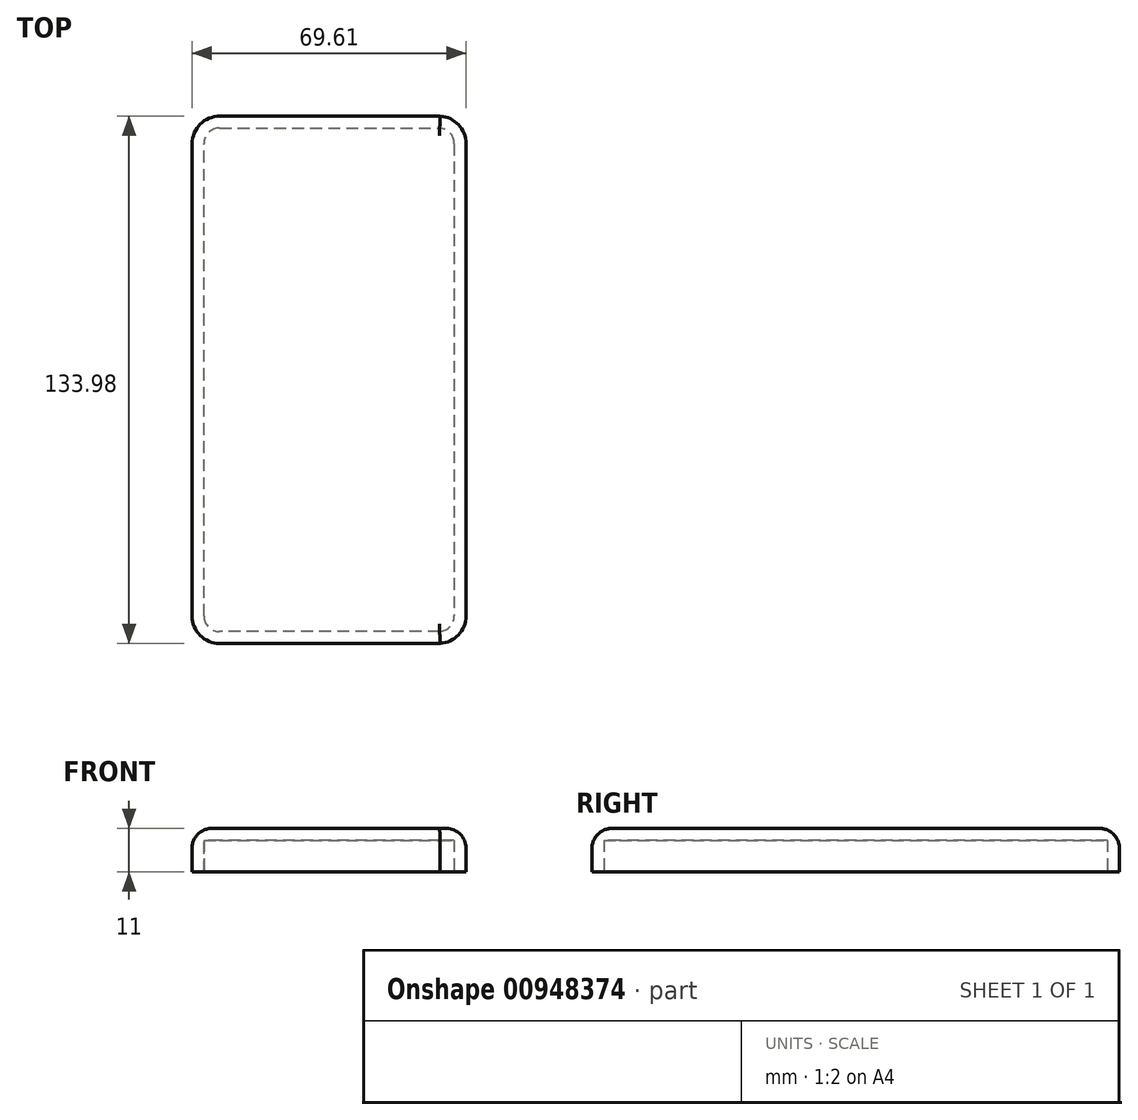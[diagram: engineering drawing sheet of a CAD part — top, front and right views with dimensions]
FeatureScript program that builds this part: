
annotation { "Feature Type Name" : "Feature", "Feature Type Description" : "" }
export const myFeature = defineFeature(function(context is Context, id is Id, definition is map)
    precondition{}
    {
        {
            var Q0;
            Q0=qCreatedBy(makeId("Top.planeOp"),FACE);
            var sketch = newSketch(context, id + "F0", { "sketchPlane" : qUnion([Q0])});
            skLineSegment(sketch, "E0", {"start": v(34.6, 0) * mm, "end": v(34.6, -60) * mm});
            skLineSegment(sketch, "E1", {"start": v(-35.02, -59.99) * mm, "end": v(-35, -0.01) * mm});
            skLineSegment(sketch, "E2", {"start": v(-0.02, -66.99) * mm, "end": v(27.98, -66.99) * mm});
            skLineSegment(sketch, "E3", {"start": v(-0.02, -66.99) * mm, "end": v(-28.02, -66.99) * mm});
            skArc(sketch, "E4", {"start": v(-35.02, -59.99) * mm, "mid": v(-32.97, -64.94) * mm, "end": v(-28.02, -66.99) * mm});
            skArc(sketch, "E5", {"start": v(27.98, -66.99) * mm, "mid": v(32.68, -64.81) * mm, "end": v(34.6, -60) * mm});
            skLineSegment(sketch, "E6", {"start": v(34.6, 0) * mm, "end": v(34.6, 60) * mm});
            skLineSegment(sketch, "E7", {"start": v(-35, -0.01) * mm, "end": v(-35, 59.99) * mm});
            skLineSegment(sketch, "E8", {"start": v(-28, 66.99) * mm, "end": v(28, 66.99) * mm});
            skArc(sketch, "E9", {"start": v(-28, 66.99) * mm, "mid": v(-32.95, 64.94) * mm, "end": v(-35, 59.99) * mm});
            skArc(sketch, "E10", {"start": v(34.6, 60) * mm, "mid": v(32.68, 64.8) * mm, "end": v(28, 66.99) * mm});
            skSolve(sketch);
        }
        {
            var Q0;
            Q0=qSketchRegion(id+"F0",true);
            extrude(context, id + "F1", {"entities" : qUnion([Q0]), "depth" : 11 * mm, "offsetDistance" : 25 * mm});
        }
        {
            var Q0;
            Q0=makeQuery(id+"F1.opExtrude","CAP_FACE",FACE,{"disambiguationData":[OSD([sQuery(id+"F0.wireOp",EDGE,"E0"),sQuery(id+"F0.wireOp",EDGE,"E1"),sQuery(id+"F0.wireOp",EDGE,"E2"),sQuery(id+"F0.wireOp",EDGE,"E3"),sQuery(id+"F0.wireOp",EDGE,"E4"),sQuery(id+"F0.wireOp",EDGE,"E5"),sQuery(id+"F0.wireOp",EDGE,"E6"),sQuery(id+"F0.wireOp",EDGE,"E7"),sQuery(id+"F0.wireOp",EDGE,"E8"),sQuery(id+"F0.wireOp",EDGE,"E9"),sQuery(id+"F0.wireOp",EDGE,"E10")])],"isStart":true});
            shell(context, id + "F2", {"entities" : qUnion([Q0]), "thickness" : 3 * mm});
        }
        {
            var Q0;
            Q0=makeQuery(id+"F1.opExtrude","CAP_FACE",FACE,{"disambiguationData":[OSD([sQuery(id+"F0.wireOp",EDGE,"E0"),sQuery(id+"F0.wireOp",EDGE,"E1"),sQuery(id+"F0.wireOp",EDGE,"E2"),sQuery(id+"F0.wireOp",EDGE,"E3"),sQuery(id+"F0.wireOp",EDGE,"E4"),sQuery(id+"F0.wireOp",EDGE,"E5"),sQuery(id+"F0.wireOp",EDGE,"E6"),sQuery(id+"F0.wireOp",EDGE,"E7"),sQuery(id+"F0.wireOp",EDGE,"E8"),sQuery(id+"F0.wireOp",EDGE,"E9"),sQuery(id+"F0.wireOp",EDGE,"E10")])],"isStart":false});
            fillet(context, id + "F3", {"entities" : qUnion([Q0]), "radius" : 5 * mm, "tangentPropagation" : true, "allowEdgeOverflow" : false});
        }
    });
